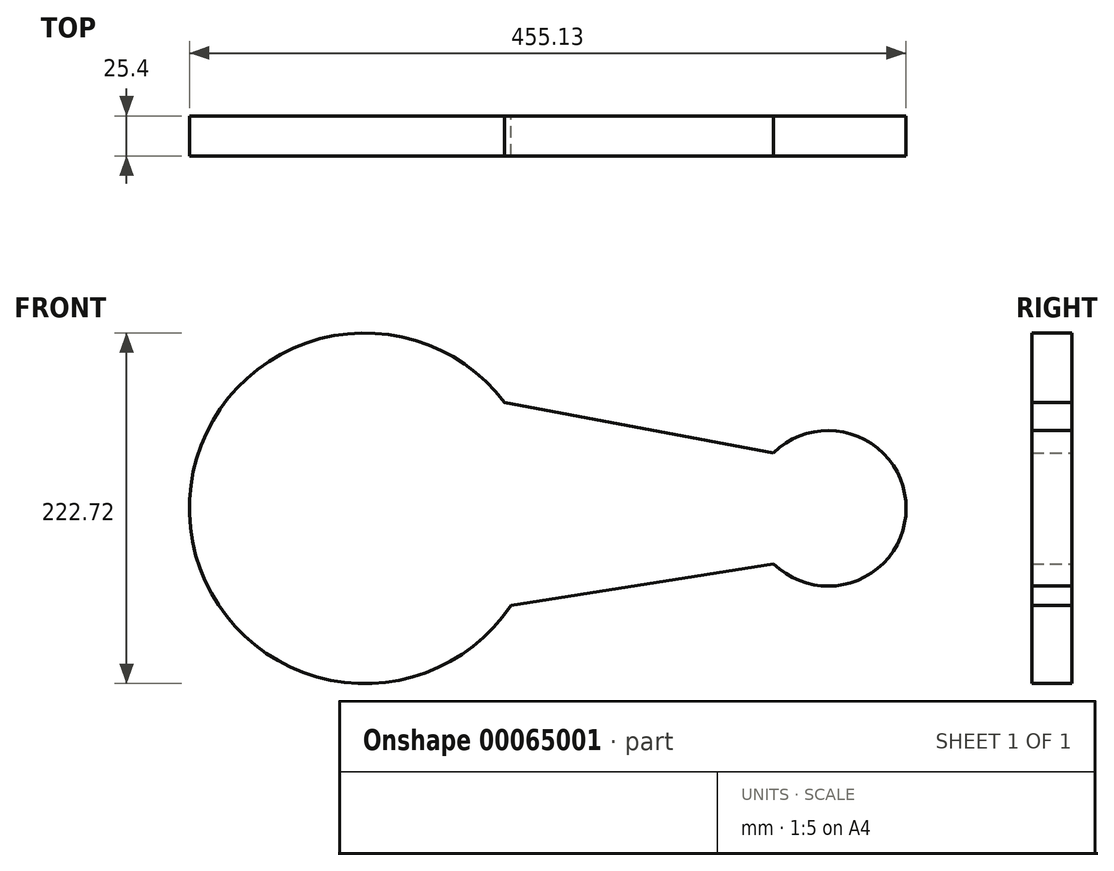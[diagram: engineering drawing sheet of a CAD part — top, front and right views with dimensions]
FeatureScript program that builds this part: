
annotation { "Feature Type Name" : "Feature", "Feature Type Description" : "" }
export const myFeature = defineFeature(function(context is Context, id is Id, definition is map)
    precondition{}
    {
        {
            var Q0;
            Q0=qCreatedBy(makeId("Front.planeOp"),FACE);
            var sketch = newSketch(context, id + "F0", { "sketchPlane" : qUnion([Q0])});
            skCircle(sketch, "E0", {"center": v(-183.27, 0) * mm, "radius": 111.36 * mm});
            skCircle(sketch, "E1", {"center": v(111.05, 0) * mm, "radius": 49.47 * mm});
            skLineSegment(sketch, "E2", {"start": v(-94.38, 67.08) * mm, "end": v(76.37, 35.28) * mm});
            skLineSegment(sketch, "E3", {"start": v(-90.5, -61.58) * mm, "end": v(76.37, -35.28) * mm});
            skSolve(sketch);
        }
        {
            var Q0;
            Q0 = qSketchRegion(id + "F0", true);
            extrude(context, id + "F1", {"entities" : qUnion([Q0]), "depth" : 25.4 * mm});
        }
    });
